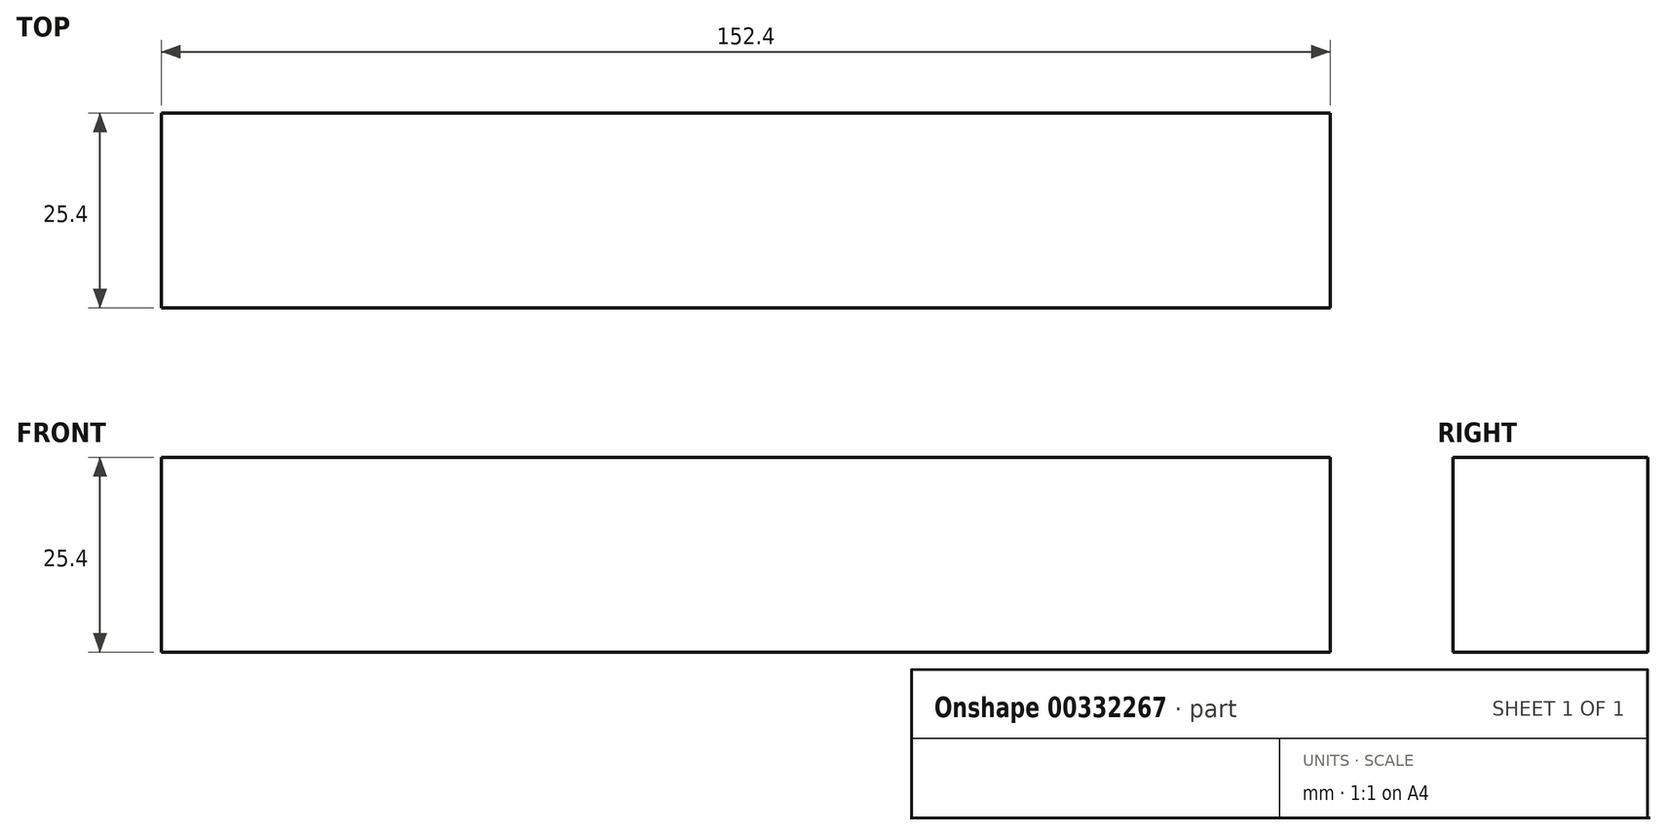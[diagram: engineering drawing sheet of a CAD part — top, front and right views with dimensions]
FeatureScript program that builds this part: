
annotation { "Feature Type Name" : "Feature", "Feature Type Description" : "" }
export const myFeature = defineFeature(function(context is Context, id is Id, definition is map)
    precondition{}
    {
        {
            var Q0;
            Q0=qCreatedBy(makeId("Front.planeOp"),FACE);
            var sketch = newSketch(context, id + "F0", { "sketchPlane" : qUnion([Q0])});
            skLineSegment(sketch, "E0.bottom", {"start": v(76.2, -12.7) * mm, "end": v(-76.2, -12.7) * mm});
            skLineSegment(sketch, "E0.top", {"start": v(76.2, 12.7) * mm, "end": v(-76.2, 12.7) * mm});
            skLineSegment(sketch, "E0.left", {"start": v(76.2, -12.7) * mm, "end": v(76.2, 12.7) * mm});
            skLineSegment(sketch, "E0.right", {"start": v(-76.2, -12.7) * mm, "end": v(-76.2, 12.7) * mm});
            skPoint(sketch, "E0.middle", {"position": v(0, 0) * mm});
            skSolve(sketch);
        }
        {
            var Q0;
            Q0=makeQuery(id+"F0.imprint","IMPRINT",FACE,{"disambiguationData":[TD([[makeQuery(id+"F0.imprint","IMPRINT",EDGE,{"derivedFrom":sQuery(id+"F0.wireOp",EDGE,"E0.bottom")}),-1.0]])]});
            extrude(context, id + "F1", {"entities" : qUnion([Q0]), "depth" : 25.4 * mm});
        }
    });
